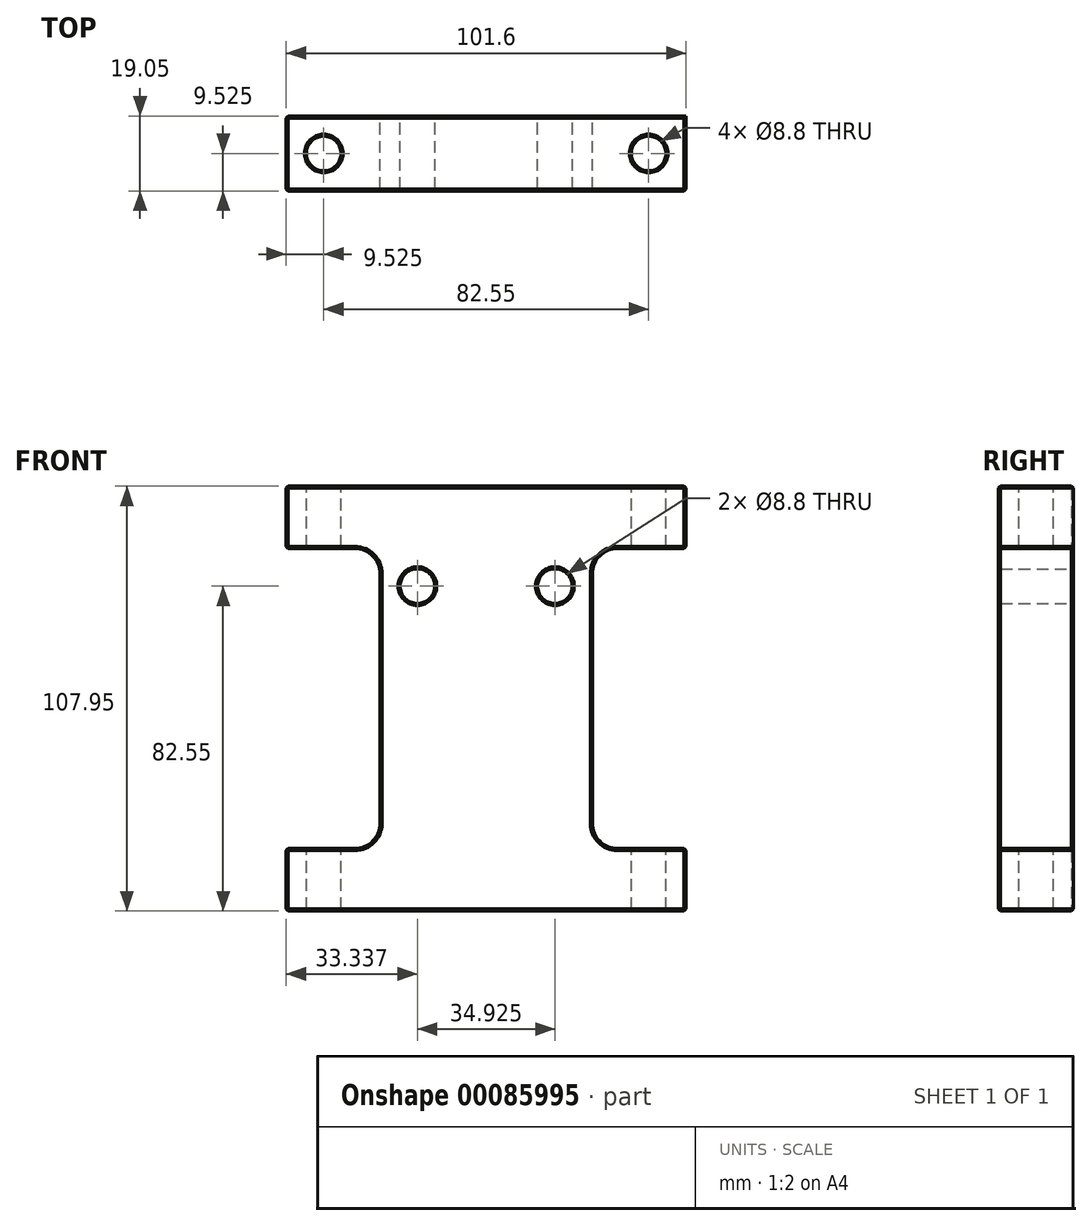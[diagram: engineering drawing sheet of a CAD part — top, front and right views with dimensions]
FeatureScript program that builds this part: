
annotation { "Feature Type Name" : "Feature", "Feature Type Description" : "" }
export const myFeature = defineFeature(function(context is Context, id is Id, definition is map)
    precondition{}
    {
        {
            var Q0;
            Q0=qCreatedBy(makeId("Front.planeOp"),FACE);
            var sketch = newSketch(context, id + "F0", { "sketchPlane" : qUnion([Q0])});
            skLineSegment(sketch, "E0", {"start": v(0, 0) * mm, "end": v(101.6, 0) * mm});
            skLineSegment(sketch, "E1", {"start": v(0, 0) * mm, "end": v(0, -15.87) * mm});
            skLineSegment(sketch, "E2", {"start": v(50.8, 0) * mm, "end": v(50.8, -53.97) * mm, "construction": true});
            skLineSegment(sketch, "E3", {"start": v(50.8, -15.87) * mm, "end": v(23.81, -15.87) * mm, "construction": true});
            skLineSegment(sketch, "E4", {"start": v(23.81, -15.87) * mm, "end": v(23.81, -53.97) * mm});
            skLineSegment(sketch, "E5", {"start": v(0, -15.87) * mm, "end": v(23.81, -15.87) * mm});
            skLineSegment(sketch, "E6", {"start": v(23.81, -53.97) * mm, "end": v(50.8, -53.97) * mm, "construction": true});
            skLineSegment(sketch, "E7.MirrorCS", {"start": v(101.6, 0) * mm, "end": v(101.6, -15.87) * mm});
            skLineSegment(sketch, "E8.MirrorCS", {"start": v(101.6, -15.87) * mm, "end": v(77.79, -15.87) * mm});
            skLineSegment(sketch, "E9.MirrorCS", {"start": v(77.79, -15.87) * mm, "end": v(77.79, -53.97) * mm});
            skLineSegment(sketch, "E10.MirrorCS", {"start": v(77.79, -53.97) * mm, "end": v(50.8, -53.97) * mm, "construction": true});
            skLineSegment(sketch, "E11.MirrorCS", {"start": v(77.79, -92.08) * mm, "end": v(77.79, -53.97) * mm});
            skLineSegment(sketch, "E12.MirrorCS", {"start": v(101.6, -92.07) * mm, "end": v(77.79, -92.07) * mm});
            skLineSegment(sketch, "E13.MirrorCS", {"start": v(101.6, -107.95) * mm, "end": v(101.6, -92.08) * mm});
            skLineSegment(sketch, "E14.MirrorCS", {"start": v(0, -107.95) * mm, "end": v(101.6, -107.95) * mm});
            skLineSegment(sketch, "E15.MirrorCS", {"start": v(0, -107.95) * mm, "end": v(0, -92.07) * mm});
            skLineSegment(sketch, "E16.MirrorCS", {"start": v(0, -92.08) * mm, "end": v(23.81, -92.07) * mm});
            skLineSegment(sketch, "E17.MirrorCS", {"start": v(23.81, -92.08) * mm, "end": v(23.81, -53.97) * mm});
            skLineSegment(sketch, "E18", {"start": v(50.8, 0) * mm, "end": v(50.8, -28.58) * mm, "construction": true});
            skLineSegment(sketch, "E19.MirrorCS", {"start": v(50.8, -107.95) * mm, "end": v(50.8, -79.37) * mm, "construction": true});
            skLineSegment(sketch, "E20", {"start": v(23.81, 0) * mm, "end": v(23.81, -25.4) * mm, "construction": true});
            skLineSegment(sketch, "E21", {"start": v(23.81, -25.4) * mm, "end": v(33.34, -25.4) * mm, "construction": true});
            skLineSegment(sketch, "E22.MirrorCS", {"start": v(77.79, -25.4) * mm, "end": v(68.26, -25.4) * mm, "construction": true});
            skSolve(sketch);
        }
        {
            var Q0;
            {var subQ0=sQuery(id+"F0.wireOp",EDGE,"E7.MirrorCS");Q0=makeQuery(id+"F0.imprint","IMPRINT",FACE,{"disambiguationData":[TD([[makeQuery(id+"F0.imprint","IMPRINT",EDGE,{"derivedFrom":subQ0}),-1.0]])]});}
            var Q1;
            {var subQ2=sQuery(id+"F0.wireOp",EDGE,"E3");Q1=makeQuery(id+"F0.imprint","IMPRINT",FACE,{"disambiguationData":[TD([[makeQuery(id+"F0.imprint","IMPRINT",EDGE,{"derivedFrom":subQ2}),1.0]])]});}
            var Q2;
            {var subQ4=sQuery(id+"F0.wireOp",EDGE,"E1");Q2=makeQuery(id+"F0.imprint","IMPRINT",FACE,{"disambiguationData":[TD([[makeQuery(id+"F0.imprint","IMPRINT",EDGE,{"derivedFrom":subQ4}),1.0]])]});}
            var Q3;
            Q3=makeQuery(id+"F0.imprint","IMPRINT",FACE,{"disambiguationData":[TD([[makeQuery(id+"F0.imprint","IMPRINT",EDGE,{"derivedFrom":sQuery(id+"F0.wireOp",EDGE,"E6")}),-1.0]])]});
            extrude(context, id + "F1", {"entities" : qUnion([Q0, Q1, Q2, Q3]), "depth" : 19.05 * mm});
        }
        {
            var Q0;
            Q0=makeQuery(id+"F1.opExtrude","SWEPT_EDGE",EDGE,{"disambiguationData":[OSD([sQuery(id+"F0.wireOp",EDGE,"E3"),sQuery(id+"F0.wireOp",EDGE,"E4"),sQuery(id+"F0.wireOp",EDGE,"E5")])]});
            var Q1;
            Q1=makeQuery(id+"F1.opExtrude","SWEPT_EDGE",EDGE,{"disambiguationData":[OSD([sQuery(id+"F0.wireOp",EDGE,"E8.MirrorCS"),sQuery(id+"F0.wireOp",EDGE,"E9.MirrorCS")])]});
            var Q2;
            Q2=makeQuery(id+"F1.opExtrude","SWEPT_EDGE",EDGE,{"disambiguationData":[OSD([sQuery(id+"F0.wireOp",EDGE,"E16.MirrorCS"),sQuery(id+"F0.wireOp",EDGE,"E17.MirrorCS")])]});
            var Q3;
            Q3=makeQuery(id+"F1.opExtrude","SWEPT_EDGE",EDGE,{"disambiguationData":[OSD([sQuery(id+"F0.wireOp",EDGE,"E11.MirrorCS"),sQuery(id+"F0.wireOp",EDGE,"E12.MirrorCS")])]});
            fillet(context, id + "F2", {"entities" : qUnion([Q0, Q1, Q2, Q3]), "radius" : 6.35 * mm, "tangentPropagation" : true, "allowEdgeOverflow" : false});
        }
        {
            var Q0;
            Q0=makeQuery(id+"F1.opExtrude","SWEPT_BODY",BODY,{"disambiguationData":[OSD([sQuery(id+"F0.wireOp",EDGE,"E0"),sQuery(id+"F0.wireOp",EDGE,"E1"),sQuery(id+"F0.wireOp",EDGE,"E4"),sQuery(id+"F0.wireOp",EDGE,"E5"),sQuery(id+"F0.wireOp",EDGE,"E7.MirrorCS"),sQuery(id+"F0.wireOp",EDGE,"E8.MirrorCS"),sQuery(id+"F0.wireOp",EDGE,"E9.MirrorCS"),sQuery(id+"F0.wireOp",EDGE,"E11.MirrorCS"),sQuery(id+"F0.wireOp",EDGE,"E12.MirrorCS"),sQuery(id+"F0.wireOp",EDGE,"E13.MirrorCS"),sQuery(id+"F0.wireOp",EDGE,"E14.MirrorCS"),sQuery(id+"F0.wireOp",EDGE,"E15.MirrorCS"),sQuery(id+"F0.wireOp",EDGE,"E16.MirrorCS"),sQuery(id+"F0.wireOp",EDGE,"E17.MirrorCS"),sQuery(id+"F0.wireOp",EDGE,"AZREb6lY-cByW-wnDT-9W0t-RmUTE3OZ0kjO"),sQuery(id+"F0.wireOp",EDGE,"d581d88e-504c-46bf-8654-af974252cbbb")])]});
            transform(context, id + "F3", {"entities" : qUnion([Q0]), "transformType" : TransformType.TRANSLATION_3D, "dx" : 0 * mm, "dy" : 0 * mm, "dz" : 0 * mm, "makeCopy" : true});
        }
        {
            var Q0;
            Q0=makeQuery(id+"F3.opPattern","COPY",BODY,{"derivedFrom":makeQuery(id+"F1.opExtrude","SWEPT_BODY",BODY,{"disambiguationData":[OSD([sQuery(id+"F0.wireOp",EDGE,"E0"),sQuery(id+"F0.wireOp",EDGE,"E1"),sQuery(id+"F0.wireOp",EDGE,"E4"),sQuery(id+"F0.wireOp",EDGE,"E5"),sQuery(id+"F0.wireOp",EDGE,"E7.MirrorCS"),sQuery(id+"F0.wireOp",EDGE,"E8.MirrorCS"),sQuery(id+"F0.wireOp",EDGE,"E9.MirrorCS"),sQuery(id+"F0.wireOp",EDGE,"E11.MirrorCS"),sQuery(id+"F0.wireOp",EDGE,"E12.MirrorCS"),sQuery(id+"F0.wireOp",EDGE,"E13.MirrorCS"),sQuery(id+"F0.wireOp",EDGE,"E14.MirrorCS"),sQuery(id+"F0.wireOp",EDGE,"E15.MirrorCS"),sQuery(id+"F0.wireOp",EDGE,"E16.MirrorCS"),sQuery(id+"F0.wireOp",EDGE,"E17.MirrorCS"),sQuery(id+"F0.wireOp",EDGE,"AZREb6lY-cByW-wnDT-9W0t-RmUTE3OZ0kjO"),sQuery(id+"F0.wireOp",EDGE,"d581d88e-504c-46bf-8654-af974252cbbb")])]}),"instanceName":"1"});
            deleteBodies(context, id + "F4", {"entities" : qUnion([Q0])});
        }
        {
            var Q0;
            Q0=qCreatedBy(makeId("Top.planeOp"),FACE);
            var sketch = newSketch(context, id + "F5", { "sketchPlane" : qUnion([Q0])});
            skCircle(sketch, "E23", {"center": v(-43.1, -20.03) * mm, "radius": 4 * mm});
            skSolve(sketch);
        }
        {
            var Q0;
            Q0=makeQuery(id+"F5.imprint","IMPRINT",FACE,{"disambiguationData":[TD([[makeQuery(id+"F5.imprint","IMPRINT",EDGE,{"derivedFrom":sQuery(id+"F5.wireOp",EDGE,"E23")}),1.0]])]});
            extrude(context, id + "F6", {"entities" : qUnion([Q0]), "oppositeDirection" : true, "depth" : 25 * mm});
        }
        {
            var Q0;
            Q0=makeQuery(id+"F6.opExtrude","CAP_FACE",FACE,{"disambiguationData":[OSD([sQuery(id+"F5.wireOp",EDGE,"E23")])],"isStart":true});
            var sketch = newSketch(context, id + "F7", { "sketchPlane" : qUnion([Q0])});
            skCircle(sketch, "E24", {"center": v(-43.1, -20.03) * mm, "radius": 6.5 * mm});
            skSolve(sketch);
        }
        {
            var Q0;
            Q0=makeQuery(id+"F7.imprint","IMPRINT",FACE,{"disambiguationData":[TD([[makeQuery(id+"F7.imprint","IMPRINT",EDGE,{"derivedFrom":makeQuery(id+"F6.opExtrude","CAP_EDGE",EDGE,{"disambiguationData":[OSD([sQuery(id+"F5.wireOp",EDGE,"E23")])],"isStart":true})}),1.0]])]});
            var Q1;
            Q1=makeQuery(id+"F7.imprint","IMPRINT",FACE,{"disambiguationData":[TD([[makeQuery(id+"F7.imprint","IMPRINT",EDGE,{"derivedFrom":sQuery(id+"F7.wireOp",EDGE,"E24")}),1.0]])]});
            extrude(context, id + "F8", {"entities" : qUnion([Q0, Q1]), "operationType" : NewBodyOperationType.ADD, "depth" : 8 * mm});
        }
        {
            var Q0;
            Q0=makeQuery(id+"F8.opExtrude","CAP_FACE",FACE,{"disambiguationData":[OSD([sQuery(id+"F7.wireOp",EDGE,"E24")])],"isStart":false});
            var sketch = newSketch(context, id + "F9", { "sketchPlane" : qUnion([Q0])});
            skLineSegment(sketch, "E25.0", {"start": v(-40.1, -18.3) * mm, "end": v(-40.1, -21.76) * mm});
            skLineSegment(sketch, "E25.1", {"start": v(-40.1, -21.76) * mm, "end": v(-43.1, -23.5) * mm});
            skLineSegment(sketch, "E25.2", {"start": v(-43.1, -23.5) * mm, "end": v(-46.1, -21.76) * mm});
            skLineSegment(sketch, "E25.3", {"start": v(-46.1, -21.76) * mm, "end": v(-46.1, -18.3) * mm});
            skLineSegment(sketch, "E25.4", {"start": v(-46.1, -18.3) * mm, "end": v(-43.1, -16.57) * mm});
            skLineSegment(sketch, "E25.5", {"start": v(-43.1, -16.57) * mm, "end": v(-40.1, -18.3) * mm});
            skPoint(sketch, "E25.0.midPoint", {"position": v(-40.1, -20.03) * mm});
            skSolve(sketch);
        }
        {
            var Q0;
            Q0=makeQuery(id+"F9.imprint","IMPRINT",FACE,{"disambiguationData":[TD([[makeQuery(id+"F9.imprint","IMPRINT",EDGE,{"derivedFrom":sQuery(id+"F9.wireOp",EDGE,"E25.0")}),-1.0]])]});
            extrude(context, id + "F10", {"entities" : qUnion([Q0]), "operationType" : NewBodyOperationType.REMOVE, "oppositeDirection" : true, "depth" : 6 * mm});
        }
        {
            var Q0;
            Q0=makeQuery(id+"F6.opExtrude","SWEPT_BODY",BODY,{"disambiguationData":[OSD([sQuery(id+"F5.wireOp",EDGE,"E23")])]});
            transform(context, id + "F11", {"entities" : qUnion([Q0]), "transformType" : TransformType.TRANSLATION_3D, "dx" : -25.4 * mm, "dy" : 0 * mm, "dz" : 0 * mm, "makeCopy" : true});
        }
        {
            var Q0;
            Q0=makeQuery(id+"F11.opPattern","COPY",FACE,{"derivedFrom":makeQuery(id+"F6.opExtrude","CAP_FACE",FACE,{"disambiguationData":[OSD([sQuery(id+"F5.wireOp",EDGE,"E23")])],"isStart":false}),"instanceName":"1"});
            extrude(context, id + "F12", {"entities" : qUnion([Q0]), "operationType" : NewBodyOperationType.REMOVE, "oppositeDirection" : true, "depth" : 5 * mm});
        }
        {
            var Q0;
            Q0=makeQuery(id+"F1.opExtrude","SWEPT_FACE",FACE,{"disambiguationData":[OSD([sQuery(id+"F0.wireOp",EDGE,"E0")])]});
            var sketch = newSketch(context, id + "F13", { "sketchPlane" : qUnion([Q0])});
            skLineSegment(sketch, "E26", {"start": v(50.8, -9.53) * mm, "end": v(9.52, -9.53) * mm});
            skPoint(sketch, "E26.startSnap0", {"position": v(0, -9.53) * mm});
            skPoint(sketch, "E26.startSnap1", {"position": v(50.8, -19.05) * mm});
            skLineSegment(sketch, "E27", {"start": v(9.52, -9.53) * mm, "end": v(92.07, -9.53) * mm});
            skSolve(sketch);
        }
        {
            var Q0;
            Q0=sQuery(id+"F13.wireOp",VERTEX,"E27.start");
            var Q1;
            Q1=sQuery(id+"F13.wireOp",VERTEX,"E27.end");
            var Q2;
            Q2=sQuery(id+"F0.wireOp",VERTEX,"E18.end");
            var Q3;
            Q3=sQuery(id+"F0.wireOp",VERTEX,"E19.MirrorCS.end");
            var Q4;
            Q4=makeQuery(id+"F1.opExtrude","SWEPT_BODY",BODY,{"disambiguationData":[OSD([sQuery(id+"F0.wireOp",EDGE,"E0"),sQuery(id+"F0.wireOp",EDGE,"E1"),sQuery(id+"F0.wireOp",EDGE,"E4"),sQuery(id+"F0.wireOp",EDGE,"E5"),sQuery(id+"F0.wireOp",EDGE,"E7.MirrorCS"),sQuery(id+"F0.wireOp",EDGE,"E8.MirrorCS"),sQuery(id+"F0.wireOp",EDGE,"E9.MirrorCS"),sQuery(id+"F0.wireOp",EDGE,"E11.MirrorCS"),sQuery(id+"F0.wireOp",EDGE,"E12.MirrorCS"),sQuery(id+"F0.wireOp",EDGE,"E13.MirrorCS"),sQuery(id+"F0.wireOp",EDGE,"E14.MirrorCS"),sQuery(id+"F0.wireOp",EDGE,"E15.MirrorCS"),sQuery(id+"F0.wireOp",EDGE,"E16.MirrorCS"),sQuery(id+"F0.wireOp",EDGE,"E17.MirrorCS"),sQuery(id+"F0.wireOp",EDGE,"AZREb6lY-cByW-wnDT-9W0t-RmUTE3OZ0kjO"),sQuery(id+"F0.wireOp",EDGE,"5702e291-1fe0-4199-8843-7c20392612490.MirrorC")])]});
            hole(context, id + "F14", {"style" : HoleStyle.SIMPLE, "endStyle" : HoleEndStyle.THROUGH, "standardTappedOrClearance" : lookupTablePath({ "standard" : "ISO", "fit" : "Normal", "size" : "M8", "type" : "Clearance" }), "standardBlindInLast" : lookupTablePath({ "fit" : "Standard", "standard" : "ISO", "size" : "M8", "type" : "Clearance" }), "holeDiameter" : 8.8 * mm, "locations" : qUnion([Q0, Q1, Q2, Q3]), "scope" : qUnion([Q4]), "isTappedThrough" : true});
        }
        {
            var Q0;
            Q0=sQuery(id+"F0.wireOp",VERTEX,"E21.end");
            var Q1;
            Q1=sQuery(id+"F0.wireOp",VERTEX,"E22.MirrorCS.end");
            var Q2;
            Q2=makeQuery(id+"F1.opExtrude","SWEPT_BODY",BODY,{"disambiguationData":[OSD([sQuery(id+"F0.wireOp",EDGE,"E0"),sQuery(id+"F0.wireOp",EDGE,"E1"),sQuery(id+"F0.wireOp",EDGE,"E4"),sQuery(id+"F0.wireOp",EDGE,"E5"),sQuery(id+"F0.wireOp",EDGE,"E7.MirrorCS"),sQuery(id+"F0.wireOp",EDGE,"E8.MirrorCS"),sQuery(id+"F0.wireOp",EDGE,"E9.MirrorCS"),sQuery(id+"F0.wireOp",EDGE,"E11.MirrorCS"),sQuery(id+"F0.wireOp",EDGE,"E12.MirrorCS"),sQuery(id+"F0.wireOp",EDGE,"E13.MirrorCS"),sQuery(id+"F0.wireOp",EDGE,"E14.MirrorCS"),sQuery(id+"F0.wireOp",EDGE,"E15.MirrorCS"),sQuery(id+"F0.wireOp",EDGE,"E16.MirrorCS"),sQuery(id+"F0.wireOp",EDGE,"E17.MirrorCS")])]});
            hole(context, id + "F15", {"style" : HoleStyle.SIMPLE, "endStyle" : HoleEndStyle.THROUGH, "oppositeDirection" : true, "standardTappedOrClearance" : lookupTablePath({ "standard" : "ISO", "fit" : "Normal", "size" : "M8", "type" : "Clearance" }), "standardBlindInLast" : lookupTablePath({ "fit" : "Standard", "standard" : "ISO", "size" : "M8", "type" : "Clearance" }), "holeDiameter" : 8.8 * mm, "locations" : qUnion([Q0, Q1]), "scope" : qUnion([Q2]), "isTappedThrough" : true});
        }
        {
            var Q0;
            Q0=makeQuery(id+"F1.opExtrude","SWEPT_FACE",FACE,{"disambiguationData":[OSD([sQuery(id+"F0.wireOp",EDGE,"E9.MirrorCS"),sQuery(id+"F0.wireOp",EDGE,"E11.MirrorCS")])]});
            var Q1;
            Q1=makeQuery(id+"F1.opExtrude","SWEPT_FACE",FACE,{"disambiguationData":[OSD([sQuery(id+"F0.wireOp",EDGE,"E8.MirrorCS")])]});
            var Q2;
            Q2=makeQuery(id+"F1.opExtrude","SWEPT_FACE",FACE,{"disambiguationData":[OSD([sQuery(id+"F0.wireOp",EDGE,"E12.MirrorCS")])]});
            var Q3;
            Q3=makeQuery(id+"F1.opExtrude","SWEPT_FACE",FACE,{"disambiguationData":[OSD([sQuery(id+"F0.wireOp",EDGE,"E14.MirrorCS")])]});
            var Q4;
            Q4=makeQuery(id+"F1.opExtrude","SWEPT_FACE",FACE,{"disambiguationData":[OSD([sQuery(id+"F0.wireOp",EDGE,"E4"),sQuery(id+"F0.wireOp",EDGE,"E17.MirrorCS")])]});
            var Q5;
            Q5=makeQuery(id+"F1.opExtrude","SWEPT_FACE",FACE,{"disambiguationData":[OSD([sQuery(id+"F0.wireOp",EDGE,"E15.MirrorCS")])]});
            var Q6;
            Q6=makeQuery(id+"F1.opExtrude","SWEPT_FACE",FACE,{"disambiguationData":[OSD([sQuery(id+"F0.wireOp",EDGE,"E1")])]});
            var Q7;
            Q7=makeQuery(id+"F1.opExtrude","SWEPT_FACE",FACE,{"disambiguationData":[OSD([sQuery(id+"F0.wireOp",EDGE,"E16.MirrorCS")])]});
            var Q8;
            Q8=makeQuery(id+"F1.opExtrude","SWEPT_FACE",FACE,{"disambiguationData":[OSD([sQuery(id+"F0.wireOp",EDGE,"E5")])]});
            var Q9;
            Q9=makeQuery(id+"F2.opFillet","BLEND_FACE",FACE,{"disambiguationData":[OSD([sQuery(id+"F0.wireOp",EDGE,"E3"),sQuery(id+"F0.wireOp",EDGE,"E4"),sQuery(id+"F0.wireOp",EDGE,"E5")])]});
            var Q10;
            Q10=makeQuery(id+"F2.opFillet","BLEND_FACE",FACE,{"disambiguationData":[OSD([sQuery(id+"F0.wireOp",EDGE,"E16.MirrorCS"),sQuery(id+"F0.wireOp",EDGE,"E17.MirrorCS")])]});
            var Q11;
            Q11=makeQuery(id+"F2.opFillet","BLEND_FACE",FACE,{"disambiguationData":[OSD([sQuery(id+"F0.wireOp",EDGE,"E8.MirrorCS"),sQuery(id+"F0.wireOp",EDGE,"E9.MirrorCS")])]});
            var Q12;
            Q12=makeQuery(id+"F2.opFillet","BLEND_FACE",FACE,{"disambiguationData":[OSD([sQuery(id+"F0.wireOp",EDGE,"E11.MirrorCS"),sQuery(id+"F0.wireOp",EDGE,"E12.MirrorCS")])]});
            var Q13;
            Q13=makeQuery(id+"F1.opExtrude","CAP_FACE",FACE,{"disambiguationData":[OSD([sQuery(id+"F0.wireOp",EDGE,"E0"),sQuery(id+"F0.wireOp",EDGE,"E1"),sQuery(id+"F0.wireOp",EDGE,"E4"),sQuery(id+"F0.wireOp",EDGE,"E5"),sQuery(id+"F0.wireOp",EDGE,"E7.MirrorCS"),sQuery(id+"F0.wireOp",EDGE,"E8.MirrorCS"),sQuery(id+"F0.wireOp",EDGE,"E9.MirrorCS"),sQuery(id+"F0.wireOp",EDGE,"E11.MirrorCS"),sQuery(id+"F0.wireOp",EDGE,"E12.MirrorCS"),sQuery(id+"F0.wireOp",EDGE,"E13.MirrorCS"),sQuery(id+"F0.wireOp",EDGE,"E14.MirrorCS"),sQuery(id+"F0.wireOp",EDGE,"E15.MirrorCS"),sQuery(id+"F0.wireOp",EDGE,"E16.MirrorCS"),sQuery(id+"F0.wireOp",EDGE,"E17.MirrorCS"),sQuery(id+"F0.wireOp",EDGE,"AZREb6lY-cByW-wnDT-9W0t-RmUTE3OZ0kjO"),sQuery(id+"F0.wireOp",EDGE,"5702e291-1fe0-4199-8843-7c20392612490.MirrorC")])],"isStart":false});
            var Q14;
            Q14=makeQuery(id+"F1.opExtrude","SWEPT_FACE",FACE,{"disambiguationData":[OSD([sQuery(id+"F0.wireOp",EDGE,"E0")])]});
            chamfer(context, id + "F16", {"entities" : qUnion([Q0, Q1, Q2, Q3, Q4, Q5, Q6, Q7, Q8, Q9, Q10, Q11, Q12, Q13, Q14]), "width" : .5 * mm, "tangentPropagation" : true});
        }
        {
            var Q0;
            Q0=makeQuery(id+"F6.opExtrude","SWEPT_BODY",BODY,{"disambiguationData":[OSD([sQuery(id+"F5.wireOp",EDGE,"E23")])]});
            deleteBodies(context, id + "F17", {"entities" : qUnion([Q0])});
        }
        {
            var Q0;
            Q0=makeQuery(id+"F11.opPattern","COPY",BODY,{"derivedFrom":makeQuery(id+"F6.opExtrude","SWEPT_BODY",BODY,{"disambiguationData":[OSD([sQuery(id+"F5.wireOp",EDGE,"E23")])]}),"instanceName":"1"});
            deleteBodies(context, id + "F18", {"entities" : qUnion([Q0])});
        }
    });
